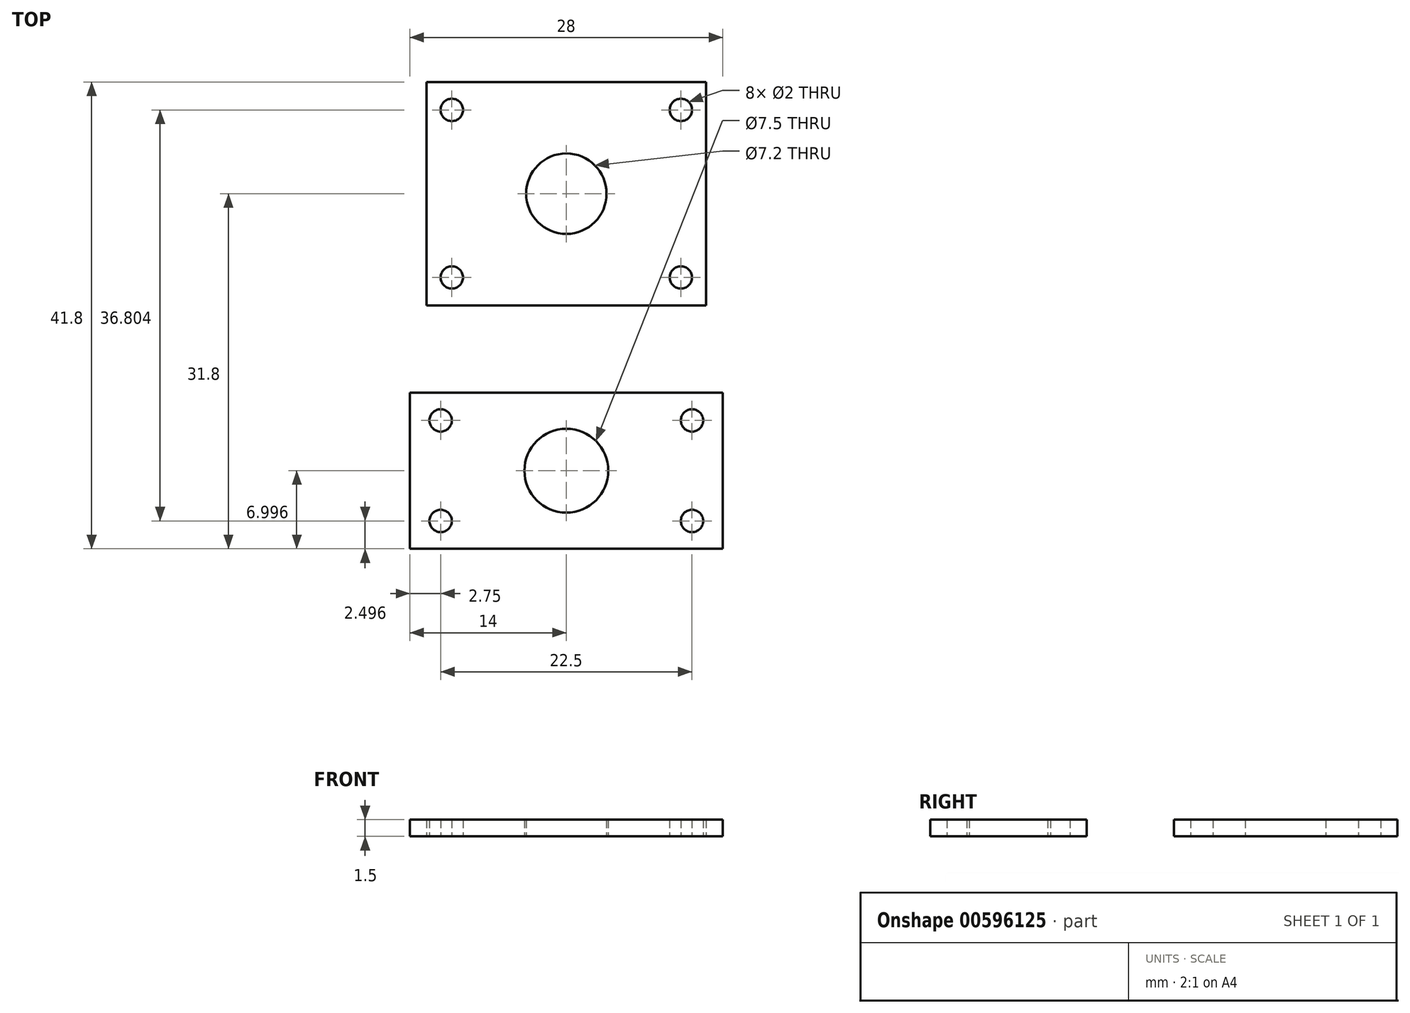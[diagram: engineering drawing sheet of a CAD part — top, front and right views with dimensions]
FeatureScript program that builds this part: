
annotation { "Feature Type Name" : "Feature", "Feature Type Description" : "" }
export const myFeature = defineFeature(function(context is Context, id is Id, definition is map)
    precondition{}
    {
        {
            var Q0;
            Q0=qCreatedBy(makeId("Top.planeOp"),FACE);
            var sketch = newSketch(context, id + "F0", { "sketchPlane" : qUnion([Q0])});
            skLineSegment(sketch, "E0.bottom", {"start": v(12.5, -10) * mm, "end": v(-12.5, -10) * mm});
            skLineSegment(sketch, "E0.top", {"start": v(12.5, 10) * mm, "end": v(-12.5, 10) * mm});
            skLineSegment(sketch, "E0.left", {"start": v(12.5, -10) * mm, "end": v(12.5, 10) * mm});
            skLineSegment(sketch, "E0.right", {"start": v(-12.5, -10) * mm, "end": v(-12.5, 10) * mm});
            skPoint(sketch, "E0.middle", {"position": v(0, 0) * mm});
            skCircle(sketch, "E1", {"center": v(-10.25, 7.5) * mm, "radius": 1 * mm});
            skCircle(sketch, "E2", {"center": v(10.25, 7.5) * mm, "radius": 1 * mm});
            skCircle(sketch, "E3", {"center": v(10.25, -7.5) * mm, "radius": 1 * mm});
            skCircle(sketch, "E4", {"center": v(-10.25, -7.5) * mm, "radius": 1 * mm});
            skCircle(sketch, "E5", {"center": v(0, 0) * mm, "radius": 3.6 * mm});
            skSolve(sketch);
        }
        {
            var Q0;
            Q0 = qSketchRegion(id + "F0", true);
            extrude(context, id + "F1", {"entities" : qUnion([Q0]), "depth" : 1.5 * mm, "offsetDistance" : 25 * mm});
        }
        {
            var Q0;
            Q0=qCreatedBy(makeId("Top.planeOp"),FACE);
            var sketch = newSketch(context, id + "F2", { "sketchPlane" : qUnion([Q0])});
            skLineSegment(sketch, "E6.bottom", {"start": v(14, -31.8) * mm, "end": v(-14, -31.8) * mm});
            skLineSegment(sketch, "E6.top", {"start": v(14, -17.8) * mm, "end": v(-14, -17.8) * mm});
            skLineSegment(sketch, "E6.left", {"start": v(14, -31.8) * mm, "end": v(14, -17.8) * mm});
            skLineSegment(sketch, "E6.right", {"start": v(-14, -31.8) * mm, "end": v(-14, -17.8) * mm});
            skPoint(sketch, "E6.middle", {"position": v(0, -24.8) * mm});
            skCircle(sketch, "E7", {"center": v(11.25, -20.3) * mm, "radius": 1 * mm});
            skCircle(sketch, "E8", {"center": v(-11.25, -20.3) * mm, "radius": 1 * mm});
            skCircle(sketch, "E9", {"center": v(-11.25, -29.3) * mm, "radius": 1 * mm});
            skCircle(sketch, "E10", {"center": v(11.25, -29.3) * mm, "radius": 1 * mm});
            skCircle(sketch, "E11", {"center": v(0, -24.8) * mm, "radius": 3.75 * mm});
            skSolve(sketch);
        }
        {
            var Q0;
            Q0 = qSketchRegion(id + "F2", true);
            extrude(context, id + "F3", {"entities" : qUnion([Q0]), "depth" : 1.5 * mm, "offsetDistance" : 25 * mm});
        }
    });
